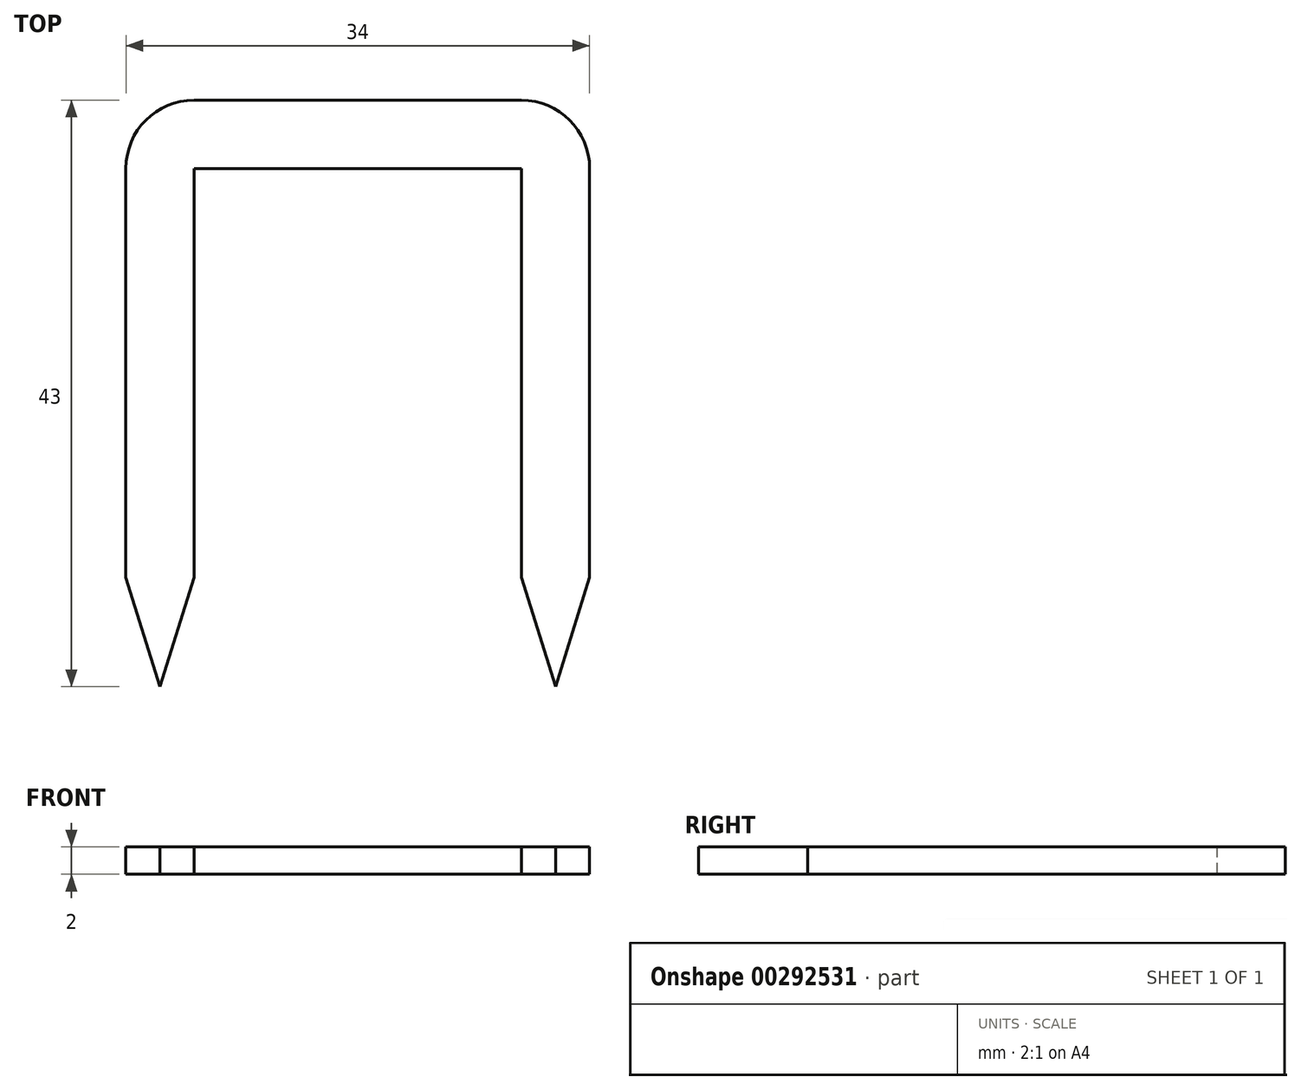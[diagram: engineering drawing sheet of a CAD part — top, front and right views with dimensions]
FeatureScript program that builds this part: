
annotation { "Feature Type Name" : "Feature", "Feature Type Description" : "" }
export const myFeature = defineFeature(function(context is Context, id is Id, definition is map)
    precondition{}
    {
        {
            var Q0;
            Q0=qCreatedBy(makeId("Top.planeOp"),FACE);
            var sketch = newSketch(context, id + "F0", { "sketchPlane" : qUnion([Q0])});
            skLineSegment(sketch, "E0", {"start": v(-11.24, -20.01) * mm, "end": v(-11.24, 9.99) * mm});
            skLineSegment(sketch, "E1", {"start": v(-6.24, 14.99) * mm, "end": v(17.76, 14.99) * mm});
            skLineSegment(sketch, "E2", {"start": v(22.76, 9.99) * mm, "end": v(22.76, -20.01) * mm});
            skLineSegment(sketch, "E3", {"start": v(22.76, -20.01) * mm, "end": v(20.26, -28.01) * mm});
            skLineSegment(sketch, "E4", {"start": v(20.26, -28.01) * mm, "end": v(17.76, -20.01) * mm});
            skLineSegment(sketch, "E5", {"start": v(17.76, -20.01) * mm, "end": v(17.76, 9.99) * mm});
            skLineSegment(sketch, "E6", {"start": v(17.76, 9.99) * mm, "end": v(-6.24, 9.99) * mm});
            skLineSegment(sketch, "E7", {"start": v(-6.24, 9.99) * mm, "end": v(-6.24, -20.01) * mm});
            skLineSegment(sketch, "E8", {"start": v(-6.24, -20.01) * mm, "end": v(-8.74, -28.01) * mm});
            skLineSegment(sketch, "E9", {"start": v(-8.74, -28.01) * mm, "end": v(-11.24, -20.01) * mm});
            skLineSegment(sketch, "E10", {"start": v(-6.24, -20.01) * mm, "end": v(-11.24, -20.01) * mm, "construction": true});
            skLineSegment(sketch, "E11", {"start": v(17.76, -20.01) * mm, "end": v(22.76, -20.01) * mm, "construction": true});
            skPoint(sketch, "E12.visualSharp", {"position": v(-11.24, 14.99) * mm});
            skArc(sketch, "E12.filletArc", {"start": v(-6.24, 14.99) * mm, "mid": v(-9.78, 13.52) * mm, "end": v(-11.24, 9.99) * mm});
            skPoint(sketch, "E13.visualSharp", {"position": v(22.76, 14.99) * mm});
            skArc(sketch, "E13.filletArc", {"start": v(22.76, 9.99) * mm, "mid": v(21.3, 13.52) * mm, "end": v(17.76, 14.99) * mm});
            skSolve(sketch);
        }
        {
            var Q0;
            Q0=makeQuery(id+"F0.imprint","IMPRINT",FACE,{"disambiguationData":[TD([[makeQuery(id+"F0.imprint","IMPRINT",EDGE,{"derivedFrom":sQuery(id+"F0.wireOp",EDGE,"E0")}),-1.0]])]});
            extrude(context, id + "F1", {"entities" : qUnion([Q0]), "depth" : 2 * mm});
        }
    });
